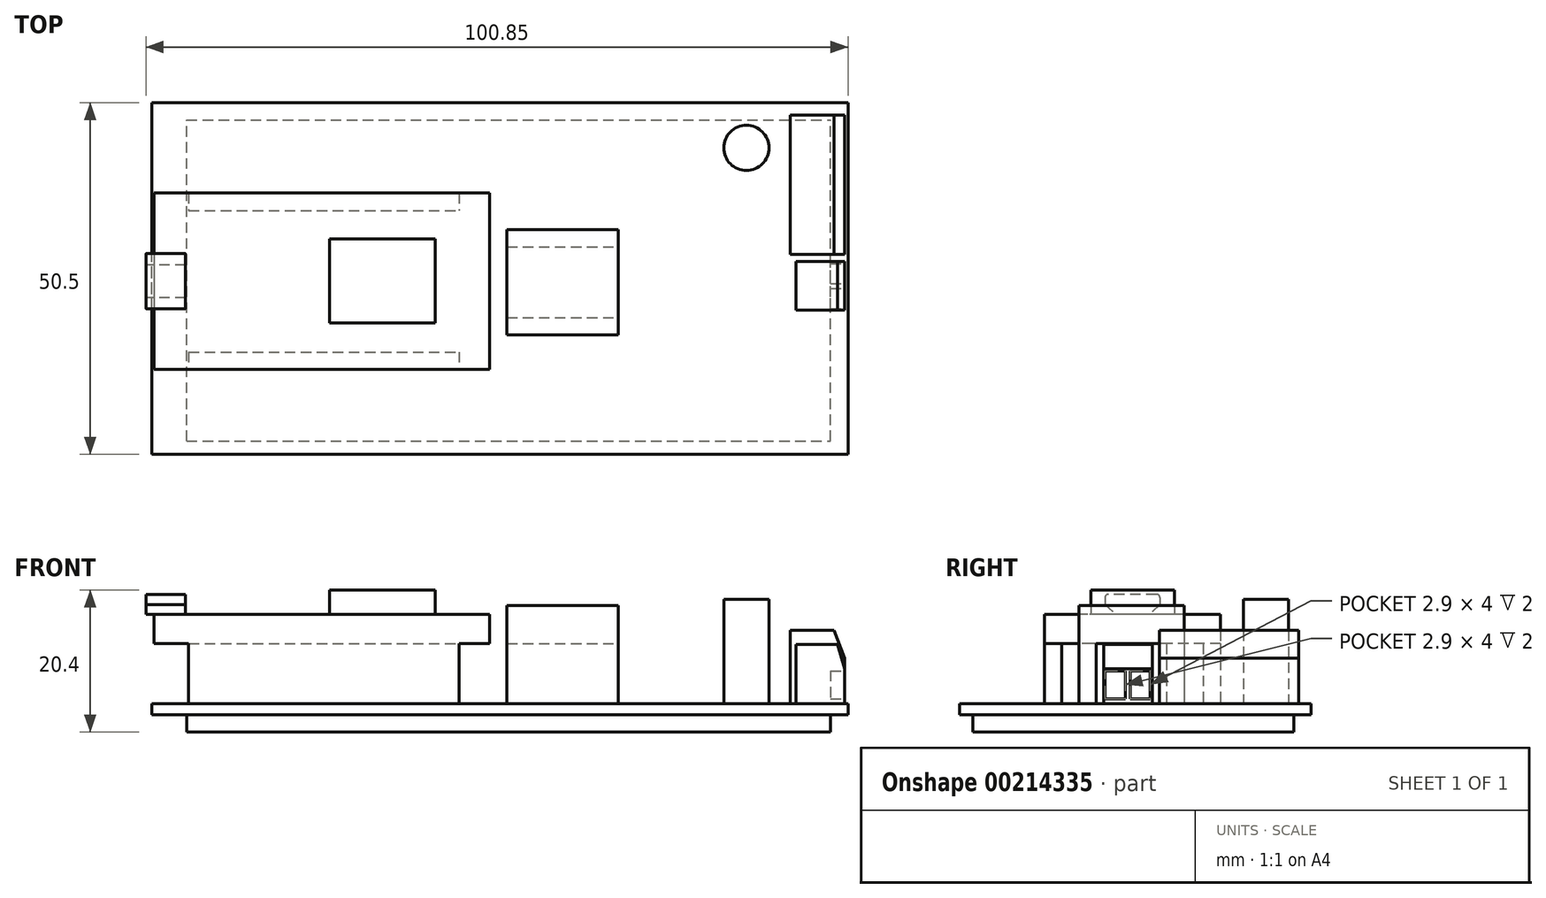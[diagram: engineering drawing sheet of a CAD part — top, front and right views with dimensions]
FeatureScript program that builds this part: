
annotation { "Feature Type Name" : "Feature", "Feature Type Description" : "" }
export const myFeature = defineFeature(function(context is Context, id is Id, definition is map)
    precondition{}
    {
        {
            var Q0;
            Q0=qCreatedBy(makeId("Top.planeOp"),FACE);
            var sketch = newSketch(context, id + "F0", { "sketchPlane" : qUnion([Q0])});
            skLineSegment(sketch, "E0.bottom", {"start": v(50, -25.25) * mm, "end": v(-50, -25.25) * mm});
            skLineSegment(sketch, "E0.top", {"start": v(50, 25.25) * mm, "end": v(-50, 25.25) * mm});
            skLineSegment(sketch, "E0.left", {"start": v(50, -25.25) * mm, "end": v(50, 25.25) * mm});
            skLineSegment(sketch, "E0.right", {"start": v(-50, -25.25) * mm, "end": v(-50, 25.25) * mm});
            skPoint(sketch, "E0.middle", {"position": v(0, 0) * mm});
            skSolve(sketch);
        }
        {
            var Q0;
            Q0=makeQuery(id+"F0.imprint","IMPRINT",FACE,{"disambiguationData":[TD([[makeQuery(id+"F0.imprint","IMPRINT",EDGE,{"derivedFrom":sQuery(id+"F0.wireOp",EDGE,"E0.bottom")}),-1.0]])]});
            extrude(context, id + "F1", {"entities" : qUnion([Q0]), "depth" : 1.6 * mm, "offsetDistance" : 25 * mm});
        }
        {
            var Q0;
            Q0=makeQuery(id+"F1.opExtrude","CAP_FACE",FACE,{"disambiguationData":[OSD([sQuery(id+"F0.wireOp",EDGE,"E0.bottom"),sQuery(id+"F0.wireOp",EDGE,"E0.top"),sQuery(id+"F0.wireOp",EDGE,"E0.left"),sQuery(id+"F0.wireOp",EDGE,"E0.right")])],"isStart":false});
            var sketch = newSketch(context, id + "F2", { "sketchPlane" : qUnion([Q0])});
            skLineSegment(sketch, "E1.bottom", {"start": v(41.7, 23.45) * mm, "end": v(49.5, 23.45) * mm});
            skLineSegment(sketch, "E1.top", {"start": v(41.7, 3.45) * mm, "end": v(49.5, 3.45) * mm});
            skLineSegment(sketch, "E1.left", {"start": v(41.7, 23.45) * mm, "end": v(41.7, 3.45) * mm});
            skLineSegment(sketch, "E1.right", {"start": v(49.5, 23.45) * mm, "end": v(49.5, 3.45) * mm});
            skLineSegment(sketch, "E2.bottom", {"start": v(49.5, 2.45) * mm, "end": v(42.5, 2.45) * mm});
            skLineSegment(sketch, "E2.top", {"start": v(49.5, -4.55) * mm, "end": v(42.5, -4.55) * mm});
            skLineSegment(sketch, "E2.left", {"start": v(49.5, 2.45) * mm, "end": v(49.5, -4.55) * mm});
            skLineSegment(sketch, "E2.right", {"start": v(42.5, 2.45) * mm, "end": v(42.5, -4.55) * mm});
            skCircle(sketch, "E3", {"center": v(35.4, 18.75) * mm, "radius": 3.25 * mm});
            skLineSegment(sketch, "E4.bottom", {"start": v(-44.7, 12.25) * mm, "end": v(-5.9, 12.25) * mm});
            skLineSegment(sketch, "E4.top", {"start": v(-44.7, 9.75) * mm, "end": v(-5.9, 9.75) * mm});
            skLineSegment(sketch, "E4.left", {"start": v(-44.7, 12.25) * mm, "end": v(-44.7, 9.75) * mm});
            skLineSegment(sketch, "E4.right", {"start": v(-5.9, 12.25) * mm, "end": v(-5.9, 9.75) * mm});
            skLineSegment(sketch, "E5.bottom", {"start": v(-44.7, -10.55) * mm, "end": v(-5.9, -10.55) * mm});
            skLineSegment(sketch, "E5.top", {"start": v(-44.7, -13.05) * mm, "end": v(-5.9, -13.05) * mm});
            skLineSegment(sketch, "E5.left", {"start": v(-44.7, -10.55) * mm, "end": v(-44.7, -13.05) * mm});
            skLineSegment(sketch, "E5.right", {"start": v(-5.9, -10.55) * mm, "end": v(-5.9, -13.05) * mm});
            skLineSegment(sketch, "E6.bottom", {"start": v(1, 7) * mm, "end": v(17, 7) * mm});
            skLineSegment(sketch, "E6.top", {"start": v(1, 4.5) * mm, "end": v(17, 4.5) * mm});
            skLineSegment(sketch, "E6.left", {"start": v(1, 7) * mm, "end": v(1, 4.5) * mm});
            skLineSegment(sketch, "E6.right", {"start": v(17, 7) * mm, "end": v(17, 4.5) * mm});
            skLineSegment(sketch, "E7.bottom", {"start": v(1, -5.6) * mm, "end": v(17, -5.6) * mm});
            skLineSegment(sketch, "E7.top", {"start": v(1, -8.1) * mm, "end": v(17, -8.1) * mm});
            skLineSegment(sketch, "E7.left", {"start": v(1, -5.6) * mm, "end": v(1, -8.1) * mm});
            skLineSegment(sketch, "E7.right", {"start": v(17, -5.6) * mm, "end": v(17, -8.1) * mm});
            skSolve(sketch);
        }
        {
            var Q0;
            Q0=makeQuery(id+"F2.imprint","IMPRINT",FACE,{"disambiguationData":[TD([[makeQuery(id+"F2.imprint","IMPRINT",EDGE,{"derivedFrom":sQuery(id+"F2.wireOp",EDGE,"E1.bottom")}),-1.0]])]});
            extrude(context, id + "F3", {"entities" : qUnion([Q0]), "operationType" : NewBodyOperationType.ADD, "depth" : 10.5 * mm, "offsetDistance" : 25 * mm});
        }
        {
            var Q0;
            Q0=makeQuery(id+"F3.opExtrude","CAP_EDGE",EDGE,{"disambiguationData":[OSD([sQuery(id+"F2.wireOp",EDGE,"E1.right")])],"isStart":false});
            chamfer(context, id + "F4", {"entities" : qUnion([Q0]), "chamferType" : ChamferType.TWO_OFFSETS, "width1" : 4 * mm, "oppositeDirection" : false, "width2" : 1.5 * mm, "tangentPropagation" : true});
        }
        {
            var Q0;
            Q0=makeQuery(id+"F2.imprint","IMPRINT",FACE,{"disambiguationData":[TD([[makeQuery(id+"F2.imprint","IMPRINT",EDGE,{"derivedFrom":sQuery(id+"F2.wireOp",EDGE,"E2.bottom")}),1.0]])]});
            extrude(context, id + "F5", {"entities" : qUnion([Q0]), "operationType" : NewBodyOperationType.ADD, "depth" : 8.5 * mm, "offsetDistance" : 25 * mm});
        }
        {
            var Q0;
            Q0=makeQuery(id+"F5.opExtrude","CAP_EDGE",EDGE,{"disambiguationData":[OSD([sQuery(id+"F2.wireOp",EDGE,"E2.left")])],"isStart":false});
            chamfer(context, id + "F6", {"entities" : qUnion([Q0]), "chamferType" : ChamferType.TWO_OFFSETS, "width1" : 3.5 * mm, "oppositeDirection" : false, "width2" : 1 * mm, "tangentPropagation" : true});
        }
        {
            var Q0;
            Q0=makeQuery(id+"F2.imprint","IMPRINT",FACE,{"disambiguationData":[TD([[makeQuery(id+"F2.imprint","IMPRINT",EDGE,{"derivedFrom":sQuery(id+"F2.wireOp",EDGE,"E3")}),1.0]])]});
            extrude(context, id + "F7", {"entities" : qUnion([Q0]), "operationType" : NewBodyOperationType.ADD, "depth" : 15 * mm, "offsetDistance" : 25 * mm});
        }
        {
            var Q0;
            Q0=makeQuery(id+"F2.imprint","IMPRINT",FACE,{"disambiguationData":[TD([[makeQuery(id+"F2.imprint","IMPRINT",EDGE,{"derivedFrom":sQuery(id+"F2.wireOp",EDGE,"E4.bottom")}),-1.0]])]});
            var Q1;
            Q1=makeQuery(id+"F2.imprint","IMPRINT",FACE,{"disambiguationData":[TD([[makeQuery(id+"F2.imprint","IMPRINT",EDGE,{"derivedFrom":sQuery(id+"F2.wireOp",EDGE,"E6.bottom")}),-1.0]])]});
            var Q2;
            Q2=makeQuery(id+"F2.imprint","IMPRINT",FACE,{"disambiguationData":[TD([[makeQuery(id+"F2.imprint","IMPRINT",EDGE,{"derivedFrom":sQuery(id+"F2.wireOp",EDGE,"E7.bottom")}),-1.0]])]});
            var Q3;
            Q3=makeQuery(id+"F2.imprint","IMPRINT",FACE,{"disambiguationData":[TD([[makeQuery(id+"F2.imprint","IMPRINT",EDGE,{"derivedFrom":sQuery(id+"F2.wireOp",EDGE,"E5.bottom")}),-1.0]])]});
            extrude(context, id + "F8", {"entities" : qUnion([Q0, Q1, Q2, Q3]), "operationType" : NewBodyOperationType.ADD, "depth" : 8.6 * mm, "offsetDistance" : 25 * mm});
        }
        {
            var Q0;
            Q0=makeQuery(id+"F1.opExtrude","CAP_FACE",FACE,{"disambiguationData":[OSD([sQuery(id+"F0.wireOp",EDGE,"E0.bottom"),sQuery(id+"F0.wireOp",EDGE,"E0.top"),sQuery(id+"F0.wireOp",EDGE,"E0.left"),sQuery(id+"F0.wireOp",EDGE,"E0.right")])],"isStart":true});
            var sketch = newSketch(context, id + "F9", { "sketchPlane" : qUnion([Q0])});
            skLineSegment(sketch, "E8.bottom", {"start": v(-45, 23.35) * mm, "end": v(47.5, 23.35) * mm});
            skLineSegment(sketch, "E8.top", {"start": v(-45, -22.75) * mm, "end": v(47.5, -22.75) * mm});
            skLineSegment(sketch, "E8.left", {"start": v(-45, 23.35) * mm, "end": v(-45, -22.75) * mm});
            skLineSegment(sketch, "E8.right", {"start": v(47.5, 23.35) * mm, "end": v(47.5, -22.75) * mm});
            skSolve(sketch);
        }
        {
            var Q0;
            Q0 = qSketchRegion(id + "F9", true);
            extrude(context, id + "F10", {"entities" : qUnion([Q0]), "operationType" : NewBodyOperationType.ADD, "depth" : 2.5 * mm, "offsetDistance" : 25 * mm});
        }
        {
            var Q0;
            Q0=makeQuery(id+"F5.opExtrude","SWEPT_FACE",FACE,{"disambiguationData":[OSD([sQuery(id+"F2.wireOp",EDGE,"E2.left")])]});
            var sketch = newSketch(context, id + "F11", { "sketchPlane" : qUnion([Q0])});
            skLineSegment(sketch, "E9.bottom", {"start": v(-4.35, 6.3) * mm, "end": v(-1.45, 6.3) * mm});
            skLineSegment(sketch, "E9.top", {"start": v(-4.35, 2.3) * mm, "end": v(-1.45, 2.3) * mm});
            skLineSegment(sketch, "E9.left", {"start": v(-4.35, 6.3) * mm, "end": v(-4.35, 2.3) * mm});
            skLineSegment(sketch, "E9.right", {"start": v(-1.45, 6.3) * mm, "end": v(-1.45, 2.3) * mm});
            skLineSegment(sketch, "E10.bottom", {"start": v(-0.75, 6.3) * mm, "end": v(2.15, 6.3) * mm});
            skLineSegment(sketch, "E10.top", {"start": v(-0.75, 2.3) * mm, "end": v(2.15, 2.3) * mm});
            skLineSegment(sketch, "E10.left", {"start": v(-0.75, 6.3) * mm, "end": v(-0.75, 2.3) * mm});
            skLineSegment(sketch, "E10.right", {"start": v(2.15, 6.3) * mm, "end": v(2.15, 2.3) * mm});
            skSolve(sketch);
        }
        {
            var Q0;
            Q0=makeQuery(id+"F11.imprint","IMPRINT",FACE,{"disambiguationData":[TD([[makeQuery(id+"F11.imprint","IMPRINT",EDGE,{"derivedFrom":sQuery(id+"F11.wireOp",EDGE,"E9.bottom")}),-1.0]])]});
            var Q1;
            Q1=makeQuery(id+"F11.imprint","IMPRINT",FACE,{"disambiguationData":[TD([[makeQuery(id+"F11.imprint","IMPRINT",EDGE,{"derivedFrom":sQuery(id+"F11.wireOp",EDGE,"E10.bottom")}),-1.0]])]});
            extrude(context, id + "F12", {"entities" : qUnion([Q0, Q1]), "operationType" : NewBodyOperationType.REMOVE, "oppositeDirection" : true, "depth" : 2 * mm, "offsetDistance" : 25 * mm});
        }
        {
            var Q0;
            Q0=makeQuery(id+"F8.opExtrude","CAP_FACE",FACE,{"disambiguationData":[OSD([sQuery(id+"F2.wireOp",EDGE,"E6.bottom"),sQuery(id+"F2.wireOp",EDGE,"E6.top"),sQuery(id+"F2.wireOp",EDGE,"E6.left"),sQuery(id+"F2.wireOp",EDGE,"E6.right")])],"isStart":false});
            var sketch = newSketch(context, id + "F13", { "sketchPlane" : qUnion([Q0])});
            skLineSegment(sketch, "E11.bottom", {"start": v(1, 7) * mm, "end": v(17, 7) * mm});
            skLineSegment(sketch, "E11.top", {"start": v(1, -8.1) * mm, "end": v(17, -8.1) * mm});
            skLineSegment(sketch, "E11.left", {"start": v(1, 7) * mm, "end": v(1, -8.1) * mm});
            skLineSegment(sketch, "E11.right", {"start": v(17, 7) * mm, "end": v(17, -8.1) * mm});
            skPoint(sketch, "E12.0", {"position": v(17, -8.1) * mm});
            skSolve(sketch);
        }
        {
            var Q0;
            Q0 = qSketchRegion(id + "F13", true);
            extrude(context, id + "F14", {"entities" : qUnion([Q0]), "operationType" : NewBodyOperationType.ADD, "depth" : 5.5 * mm, "offsetDistance" : 25 * mm});
        }
        {
            var Q0;
            Q0=makeQuery(id+"F8.opExtrude","CAP_FACE",FACE,{"disambiguationData":[OSD([sQuery(id+"F2.wireOp",EDGE,"E4.bottom"),sQuery(id+"F2.wireOp",EDGE,"E4.top"),sQuery(id+"F2.wireOp",EDGE,"E4.left"),sQuery(id+"F2.wireOp",EDGE,"E4.right")])],"isStart":false});
            var sketch = newSketch(context, id + "F15", { "sketchPlane" : qUnion([Q0])});
            skLineSegment(sketch, "E13.bottom", {"start": v(-49.7, 12.25) * mm, "end": v(-1.5, 12.25) * mm});
            skLineSegment(sketch, "E13.top", {"start": v(-49.7, -13.05) * mm, "end": v(-1.5, -13.05) * mm});
            skLineSegment(sketch, "E13.left", {"start": v(-49.7, 12.25) * mm, "end": v(-49.7, -13.05) * mm});
            skLineSegment(sketch, "E13.right", {"start": v(-1.5, 12.25) * mm, "end": v(-1.5, -13.05) * mm});
            skSolve(sketch);
        }
        {
            var Q0;
            Q0 = qSketchRegion(id + "F15", true);
            extrude(context, id + "F16", {"entities" : qUnion([Q0]), "operationType" : NewBodyOperationType.ADD, "depth" : 4.2 * mm, "offsetDistance" : 25 * mm});
        }
        {
            var Q0;
            Q0=makeQuery(id+"F16.opExtrude","CAP_FACE",FACE,{"disambiguationData":[OSD([sQuery(id+"F15.wireOp",EDGE,"E13.bottom"),sQuery(id+"F15.wireOp",EDGE,"E13.top"),sQuery(id+"F15.wireOp",EDGE,"E13.left"),sQuery(id+"F15.wireOp",EDGE,"E13.right")])],"isStart":false});
            var sketch = newSketch(context, id + "F17", { "sketchPlane" : qUnion([Q0])});
            skLineSegment(sketch, "E14.bottom", {"start": v(-24.46, 5.65) * mm, "end": v(-9.3, 5.65) * mm});
            skLineSegment(sketch, "E14.top", {"start": v(-24.46, -6.41) * mm, "end": v(-9.3, -6.41) * mm});
            skLineSegment(sketch, "E14.left", {"start": v(-24.46, 5.65) * mm, "end": v(-24.46, -6.41) * mm});
            skLineSegment(sketch, "E14.right", {"start": v(-9.3, 5.65) * mm, "end": v(-9.3, -6.41) * mm});
            skSolve(sketch);
        }
        {
            var Q0;
            Q0=makeQuery(id+"F17.imprint","IMPRINT",FACE,{"disambiguationData":[TD([[makeQuery(id+"F17.imprint","IMPRINT",EDGE,{"derivedFrom":sQuery(id+"F17.wireOp",EDGE,"E14.bottom")}),-1.0]])]});
            extrude(context, id + "F18", {"entities" : qUnion([Q0]), "operationType" : NewBodyOperationType.ADD, "depth" : 3.5 * mm, "offsetDistance" : 25 * mm});
        }
        {
            var Q0;
            Q0=makeQuery(id+"F16.opExtrude","CAP_FACE",FACE,{"disambiguationData":[OSD([sQuery(id+"F15.wireOp",EDGE,"E13.bottom"),sQuery(id+"F15.wireOp",EDGE,"E13.top"),sQuery(id+"F15.wireOp",EDGE,"E13.left"),sQuery(id+"F15.wireOp",EDGE,"E13.right")])],"isStart":false});
            var sketch = newSketch(context, id + "F19", { "sketchPlane" : qUnion([Q0])});
            skLineSegment(sketch, "E15.bottom", {"start": v(-50.85, 3.55) * mm, "end": v(-45.15, 3.55) * mm});
            skLineSegment(sketch, "E15.top", {"start": v(-50.85, -4.35) * mm, "end": v(-45.15, -4.35) * mm});
            skLineSegment(sketch, "E15.left", {"start": v(-50.85, 3.55) * mm, "end": v(-50.85, -4.35) * mm});
            skLineSegment(sketch, "E15.right", {"start": v(-45.15, 3.55) * mm, "end": v(-45.15, -4.35) * mm});
            skLineSegment(sketch, "E16", {"start": v(-56.62, -0.4) * mm, "end": v(13.05, -0.4) * mm, "construction": true});
            skSolve(sketch);
        }
        {
            var Q0;
            Q0 = qSketchRegion(id + "F19", true);
            extrude(context, id + "F20", {"entities" : qUnion([Q0]), "operationType" : NewBodyOperationType.ADD, "depth" : 2.9 * mm, "offsetDistance" : 25 * mm});
        }
        {
            var Q0;
            Q0=makeQuery(id+"F20.opExtrude","SWEPT_FACE",FACE,{"disambiguationData":[OSD([sQuery(id+"F19.wireOp",EDGE,"E15.left")])]});
            var sketch = newSketch(context, id + "F21", { "sketchPlane" : qUnion([Q0])});
            skLineSegment(sketch, "E17", {"start": v(4.35, 15.8) * mm, "end": v(2.75, 14.4) * mm});
            skLineSegment(sketch, "E18", {"start": v(2.75, 14.4) * mm, "end": v(4.35, 14.4) * mm});
            skLineSegment(sketch, "E19", {"start": v(4.35, 14.4) * mm, "end": v(4.35, 15.8) * mm});
            skLineSegment(sketch, "E20", {"start": v(-3.55, 14.4) * mm, "end": v(-3.55, 15.8) * mm});
            skLineSegment(sketch, "E21", {"start": v(-3.55, 15.8) * mm, "end": v(-1.95, 14.4) * mm});
            skLineSegment(sketch, "E22", {"start": v(-1.95, 14.4) * mm, "end": v(-3.55, 14.4) * mm});
            skLineSegment(sketch, "E23", {"start": v(0.4, 19.31) * mm, "end": v(0.4, 11.06) * mm, "construction": true});
            skSolve(sketch);
        }
        {
            var Q0;
            Q0 = qSketchRegion(id + "F21", true);
            extrude(context, id + "F22", {"entities" : qUnion([Q0]), "operationType" : NewBodyOperationType.REMOVE, "endBound" : BoundingType.UP_TO_NEXT, "oppositeDirection" : true, "depth" : 25 * mm, "offsetDistance" : 25 * mm});
        }
        {
            var Q0;
            Q0=makeQuery(id+"F22.boolean.opBoolean","COPY",EDGE,{"derivedFrom":makeQuery(id+"F22.opExtrude","SWEPT_EDGE",EDGE,{"disambiguationData":[OSD([sQuery(id+"F19.wireOp",EDGE,"E15.bottom"),sQuery(id+"F19.wireOp",EDGE,"E15.left"),sQuery(id+"F21.wireOp",EDGE,"E20"),sQuery(id+"F21.wireOp",EDGE,"E21")])]})});
            var Q1;
            Q1=makeQuery(id+"F20.opExtrude","CAP_EDGE",EDGE,{"disambiguationData":[OSD([sQuery(id+"F19.wireOp",EDGE,"E15.bottom")])],"isStart":false});
            var Q2;
            Q2=makeQuery(id+"F20.opExtrude","CAP_EDGE",EDGE,{"disambiguationData":[OSD([sQuery(id+"F19.wireOp",EDGE,"E15.top")])],"isStart":false});
            var Q3;
            Q3=makeQuery(id+"F22.boolean.opBoolean","COPY",EDGE,{"derivedFrom":makeQuery(id+"F22.opExtrude","SWEPT_EDGE",EDGE,{"disambiguationData":[OSD([sQuery(id+"F19.wireOp",EDGE,"E15.top"),sQuery(id+"F19.wireOp",EDGE,"E15.left"),sQuery(id+"F21.wireOp",EDGE,"E17"),sQuery(id+"F21.wireOp",EDGE,"E19")])]})});
            fillet(context, id + "F23", {"entities" : qUnion([Q0, Q1, Q2, Q3]), "tangentPropagation" : true, "radius" : 0.5 * mm, "defaultsChanged" : true, "vertexSettings" : [], "allowEdgeOverflow" : false});
        }
    });
